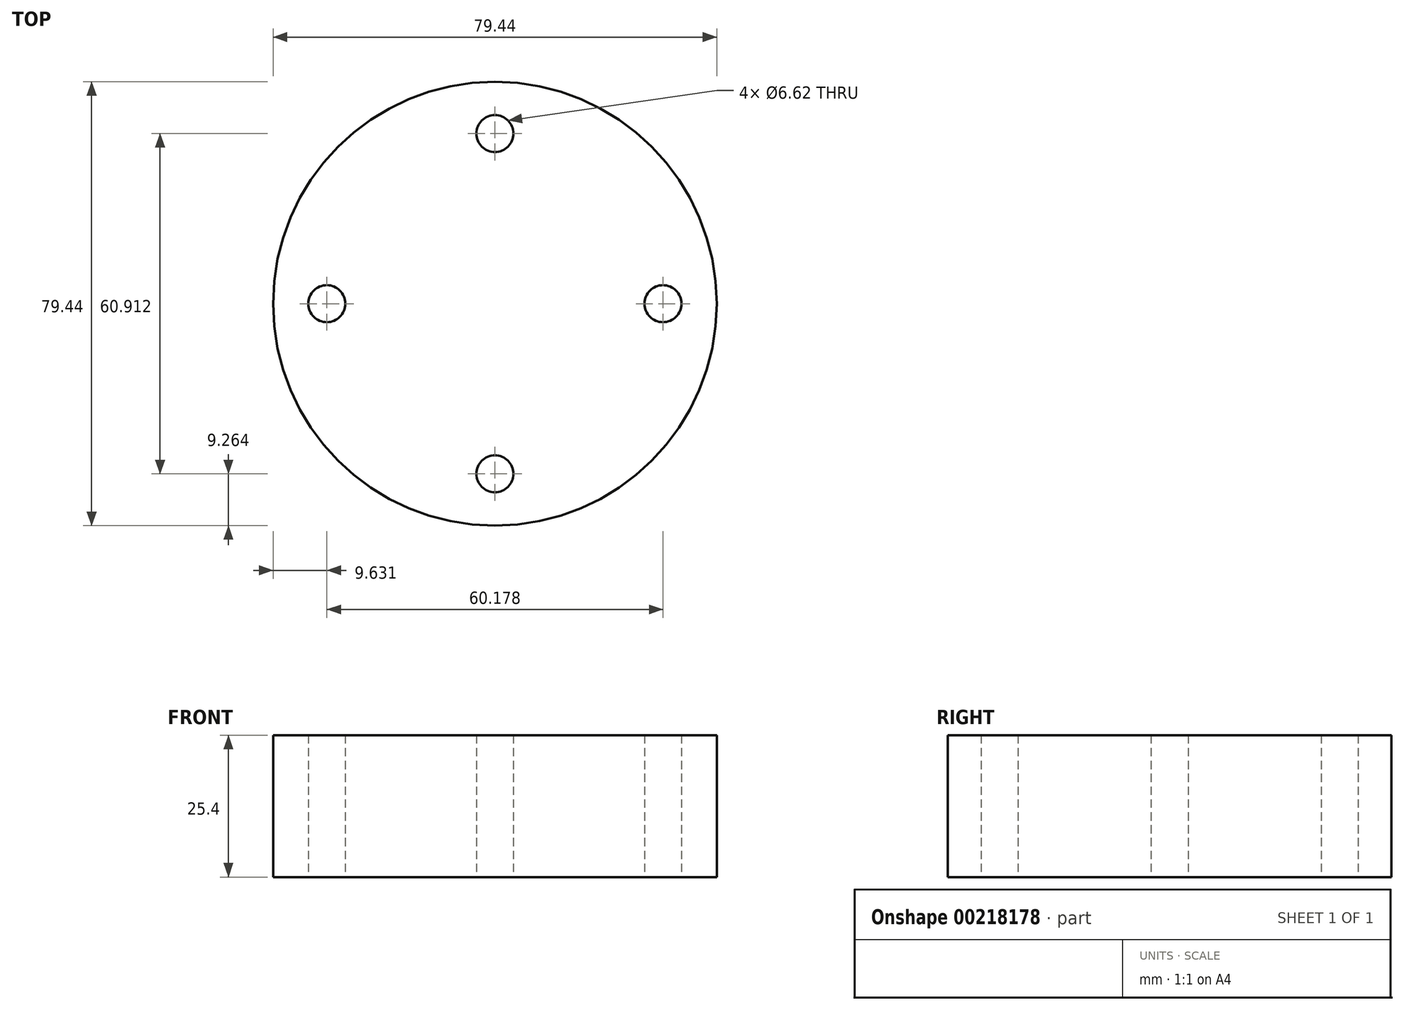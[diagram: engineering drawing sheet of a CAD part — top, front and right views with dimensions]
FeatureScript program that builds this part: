
annotation { "Feature Type Name" : "Feature", "Feature Type Description" : "" }
export const myFeature = defineFeature(function(context is Context, id is Id, definition is map)
    precondition{}
    {
        {
            var Q0;
            Q0=qCreatedBy(makeId("Top.planeOp"),FACE);
            var sketch = newSketch(context, id + "F0", { "sketchPlane" : qUnion([Q0])});
            skCircle(sketch, "E0", {"center": v(0, 0) * mm, "radius": 39.72 * mm});
            skCircle(sketch, "E1", {"center": v(30.09, 0) * mm, "radius": 3.31 * mm});
            skCircle(sketch, "E2", {"center": v(0, 30.46) * mm, "radius": 3.31 * mm});
            skCircle(sketch, "E3", {"center": v(-30.09, 0) * mm, "radius": 3.31 * mm});
            skCircle(sketch, "E4", {"center": v(0, -30.46) * mm, "radius": 3.31 * mm});
            skSolve(sketch);
        }
        {
            var Q0;
            Q0=makeQuery(id+"F0.imprint","IMPRINT",FACE,{"disambiguationData":[TD([[makeQuery(id+"F0.imprint","IMPRINT",EDGE,{"derivedFrom":sQuery(id+"F0.wireOp",EDGE,"E0")}),1.0]])]});
            extrude(context, id + "F1", {"entities" : qUnion([Q0]), "depth" : 25.4 * mm});
        }
    });
